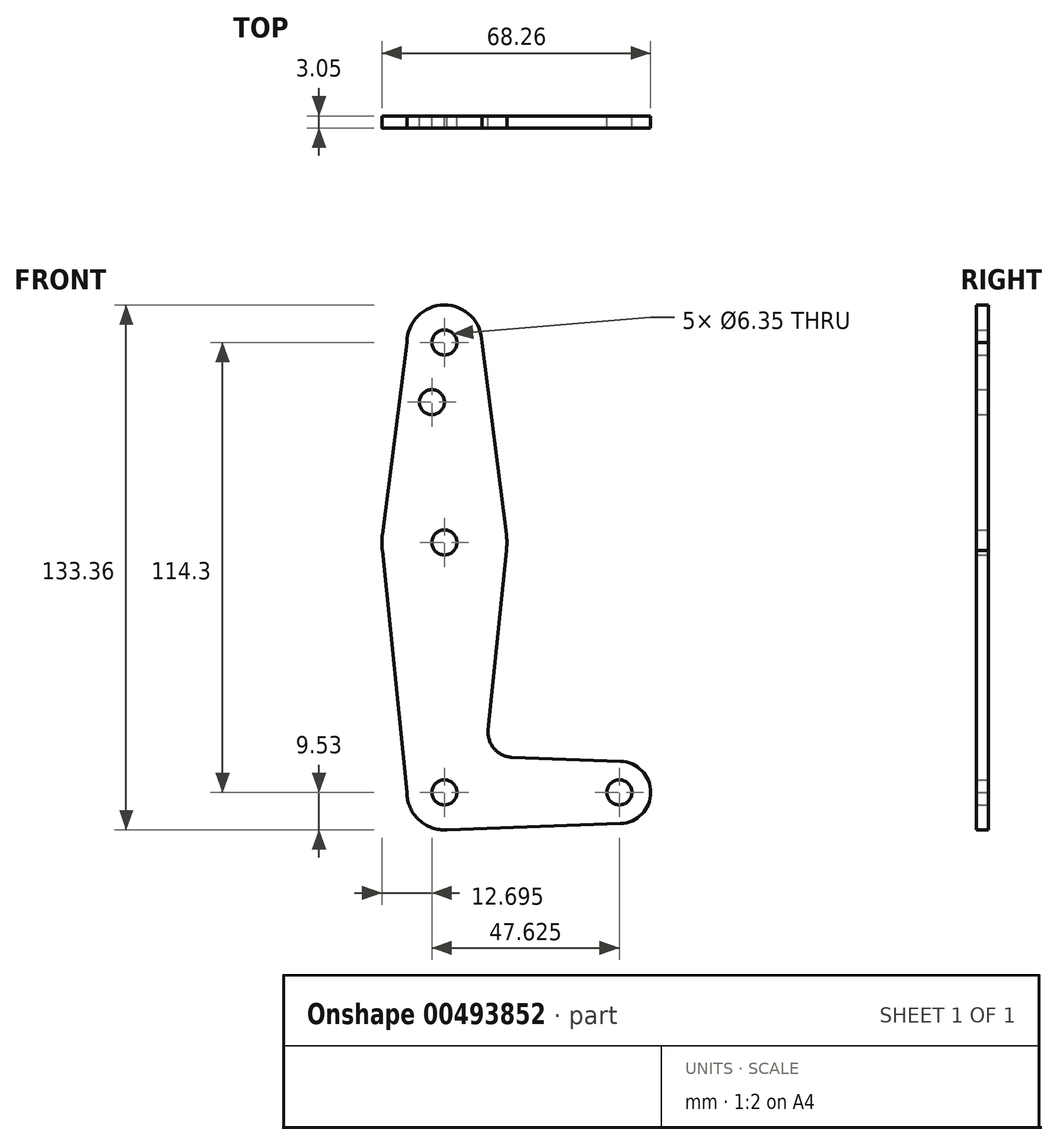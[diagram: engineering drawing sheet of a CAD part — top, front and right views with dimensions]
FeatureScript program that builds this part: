
annotation { "Feature Type Name" : "Feature", "Feature Type Description" : "" }
export const myFeature = defineFeature(function(context is Context, id is Id, definition is map)
    precondition{}
    {
        {
            var Q0;
            Q0=qCreatedBy(makeId("Front.planeOp"),FACE);
            var sketch = newSketch(context, id + "F0", { "sketchPlane" : qUnion([Q0])});
            skLineSegment(sketch, "E0", {"start": v(0, 0) * mm, "end": v(0, 114.3) * mm, "construction": true});
            skLineSegment(sketch, "E1", {"start": v(0, 0) * mm, "end": v(44.45, 0) * mm, "construction": true});
            skCircle(sketch, "E2", {"center": v(0, 114.3) * mm, "radius": 9.53 * mm});
            skCircle(sketch, "E3", {"center": v(0, 0) * mm, "radius": 9.53 * mm});
            skCircle(sketch, "E4", {"center": v(44.45, 0) * mm, "radius": 7.94 * mm});
            skLineSegment(sketch, "E5", {"start": v(0, -9.53) * mm, "end": v(44.73, -7.93) * mm});
            skCircle(sketch, "E6", {"center": v(0, 114.3) * mm, "radius": 3.17 * mm});
            skCircle(sketch, "E7", {"center": v(0, 0) * mm, "radius": 3.18 * mm});
            skCircle(sketch, "E8", {"center": v(44.45, 0) * mm, "radius": 3.18 * mm});
            skCircle(sketch, "E9", {"center": v(-3.18, 99.14) * mm, "radius": 3.18 * mm});
            skCircle(sketch, "E10", {"center": v(0, 63.5) * mm, "radius": 15.88 * mm});
            skCircle(sketch, "E11", {"center": v(0, 63.5) * mm, "radius": 3.17 * mm});
            skLineSegment(sketch, "E12", {"start": v(-9.53, 114.3) * mm, "end": v(-15.75, 65.5) * mm});
            skLineSegment(sketch, "E13", {"start": v(9.53, 114.3) * mm, "end": v(15.75, 65.5) * mm});
            skLineSegment(sketch, "E14", {"start": v(-15.75, 61.5) * mm, "end": v(-9.53, 0) * mm});
            skLineSegment(sketch, "E15", {"start": v(44.73, 7.93) * mm, "end": v(17.22, 8.92) * mm});
            skPoint(sketch, "E16.newPointA", {"position": v(9.53, 0) * mm});
            skPoint(sketch, "E16.newPointB", {"position": v(0, 9.53) * mm});
            skPoint(sketch, "E17.visualSharp", {"position": v(11.13, 15.9) * mm});
            skArc(sketch, "E17.filletArc", {"start": v(11.13, 15.9) * mm, "mid": v(11.13, 14.64) * mm, "end": v(11.38, 13.4) * mm});
            skLineSegment(sketch, "E18", {"start": v(15.75, 61.5) * mm, "end": v(11.13, 15.9) * mm});
            skArc(sketch, "E19", {"start": v(11.38, 13.4) * mm, "mid": v(13.58, 10.22) * mm, "end": v(17.22, 8.92) * mm});
            skSolve(sketch);
        }
        {
            var Q0;
            Q0 = qSketchRegion(id + "F0", true);
            extrude(context, id + "F1", {"entities" : qUnion([Q0]), "depth" : 3.05 * mm});
        }
    });
